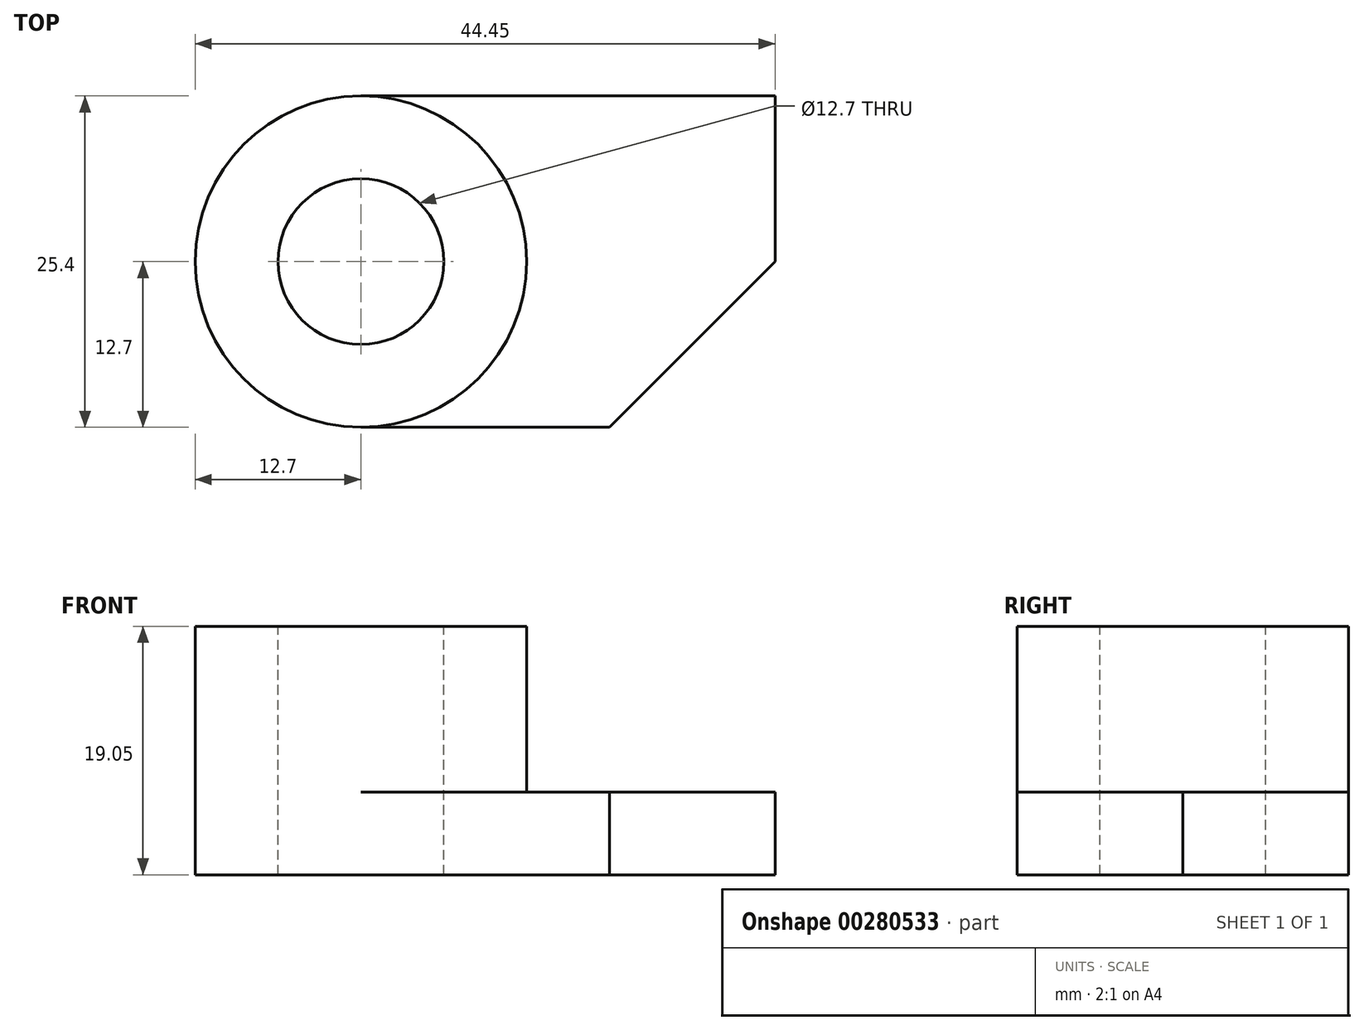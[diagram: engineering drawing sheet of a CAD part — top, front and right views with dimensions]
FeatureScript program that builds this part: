
annotation { "Feature Type Name" : "Feature", "Feature Type Description" : "" }
export const myFeature = defineFeature(function(context is Context, id is Id, definition is map)
    precondition{}
    {
        {
            var Q0;
            Q0=qCreatedBy(makeId("Top.planeOp"),FACE);
            var sketch = newSketch(context, id + "F0", { "sketchPlane" : qUnion([Q0])});
            skCircle(sketch, "E0", {"center": v(0, 0) * mm, "radius": 12.7 * mm});
            skSolve(sketch);
        }
        {
            var Q0;
            Q0 = qSketchRegion(id + "F0", true);
            extrude(context, id + "F1", {"entities" : qUnion([Q0]), "depth" : 19.05 * mm});
        }
        {
            var Q0;
            Q0=makeQuery(id+"F1.opExtrude","CAP_FACE",FACE,{"disambiguationData":[OSD([sQuery(id+"F0.wireOp",EDGE,"E0")])],"isStart":false});
            var sketch = newSketch(context, id + "F2", { "sketchPlane" : qUnion([Q0])});
            skCircle(sketch, "E1", {"center": v(0, 0) * mm, "radius": 6.35 * mm});
            skSolve(sketch);
        }
        {
            var Q0;
            Q0 = qSketchRegion(id + "F2", true);
            extrude(context, id + "F3", {"entities" : qUnion([Q0]), "operationType" : NewBodyOperationType.REMOVE, "oppositeDirection" : true, "depth" : 25.4 * mm});
        }
        {
            var Q0;
            Q0=qCreatedBy(makeId("Top.planeOp"),FACE);
            var sketch = newSketch(context, id + "F4", { "sketchPlane" : qUnion([Q0])});
            skLineSegment(sketch, "E2", {"start": v(0, 12.7) * mm, "end": v(31.75, 12.7) * mm});
            skLineSegment(sketch, "E3", {"start": v(31.75, 12.7) * mm, "end": v(31.75, 0) * mm});
            skLineSegment(sketch, "E4", {"start": v(31.75, 0) * mm, "end": v(19.05, -12.7) * mm});
            skLineSegment(sketch, "E5", {"start": v(19.05, -12.7) * mm, "end": v(0, -12.7) * mm});
            skLineSegment(sketch, "E6", {"start": v(0, -12.7) * mm, "end": v(0, 12.7) * mm});
            skSolve(sketch);
        }
        {
            var Q0;
            Q0 = qSketchRegion(id + "F4", true);
            extrude(context, id + "F5", {"entities" : qUnion([Q0]), "operationType" : NewBodyOperationType.ADD, "depth" : 6.35 * mm});
        }
        {
            var Q0;
            {var subQ0=sQuery(id+"F4.wireOp",EDGE,"E6");Q0=makeQuery(id+"F5.boolean.opBoolean","SPLIT",FACE,{"disambiguationData":[TD([makeQuery(id+"F3.boolean.opBoolean","COPY",FACE,{"derivedFrom":makeQuery(id+"F3.opExtrude","SWEPT_FACE",FACE,{"disambiguationData":[OSD([sQuery(id+"F2.wireOp",EDGE,"E1")])]})})])],"derivedFrom":makeQuery(id+"F5.opExtrude","CAP_FACE",FACE,{"disambiguationData":[OSD([sQuery(id+"F4.wireOp",EDGE,"E2"),sQuery(id+"F4.wireOp",EDGE,"E3"),sQuery(id+"F4.wireOp",EDGE,"E4"),sQuery(id+"F4.wireOp",EDGE,"E5"),subQ0])],"isStart":false})});}
            var sketch = newSketch(context, id + "F6", { "sketchPlane" : qUnion([Q0])});
            skLineSegment(sketch, "E7", {"start": v(0, -6.35) * mm, "end": v(0, 6.35) * mm});
            skArc(sketch, "E8", {"start": v(0, -6.35) * mm, "mid": v(6.35, 0) * mm, "end": v(0, 6.35) * mm});
            skSolve(sketch);
        }
        {
            var Q0;
            Q0 = qSketchRegion(id + "F6", true);
            extrude(context, id + "F7", {"entities" : qUnion([Q0]), "operationType" : NewBodyOperationType.REMOVE, "endBound" : BoundingType.SYMMETRIC, "depth" : 76.2 * mm});
        }
    });
